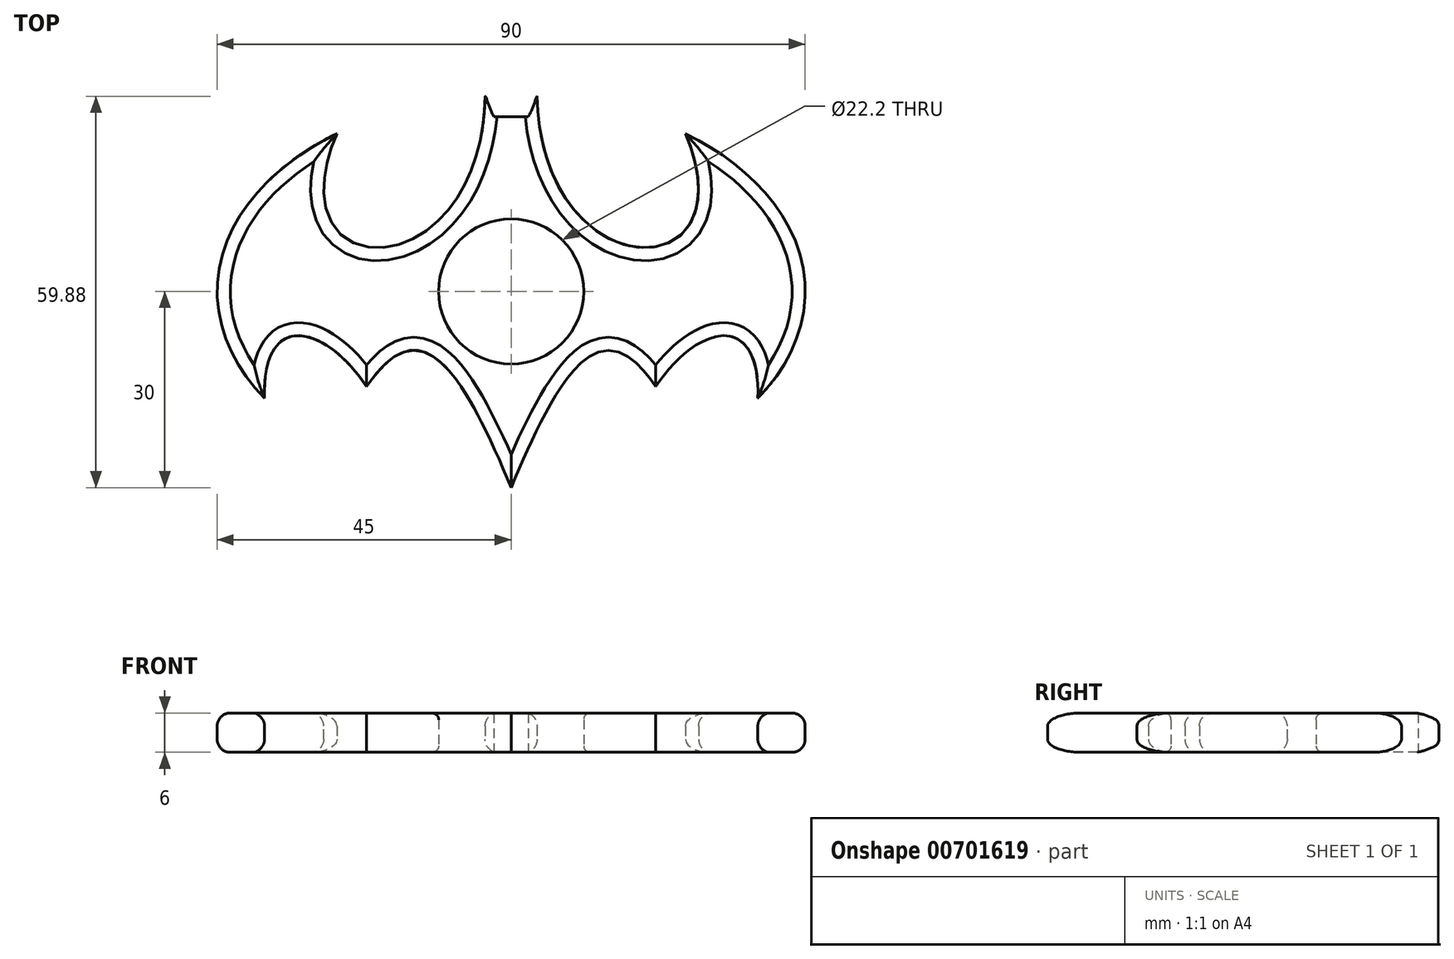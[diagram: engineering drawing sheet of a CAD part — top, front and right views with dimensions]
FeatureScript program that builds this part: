
annotation { "Feature Type Name" : "Feature", "Feature Type Description" : "" }
export const myFeature = defineFeature(function(context is Context, id is Id, definition is map)
    precondition{}
    {
        {
            var Q0;
            Q0=qCreatedBy(makeId("Top.planeOp"),FACE);
            var sketch = newSketch(context, id + "F0", { "sketchPlane" : qUnion([Q0])});
            skCircle(sketch, "E0", {"center": v(0, 0) * mm, "radius": 11.1 * mm});
            skEllipticalArc(sketch, "E1", {});
            skFitSpline(sketch, "E2", {"points": [v(-26.68, 24.16) * mm, v(-3.98, 29.88) * mm], "startDerivative": vector(-30.78, -72.47) * mm, "endDerivative": vector(1.92, 89.65) * mm});
            skFitSpline(sketch, "E3", {"points": [v(-3.98, 29.88) * mm, v(-2.62, 26.73) * mm], "startDerivative": vector(0.9, -0.78) * mm, "endDerivative": vector(3.17, -5.82) * mm});
            skLineSegment(sketch, "E4", {"start": v(-2.62, 26.73) * mm, "end": v(0, 26.73) * mm});
            skFitSpline(sketch, "E5", {"points": [v(-37.75, -16.33) * mm, v(-22.12, -14.55) * mm], "startDerivative": vector(-1.4, 39.24) * mm, "endDerivative": vector(20.6, -30.22) * mm});
            skFitSpline(sketch, "E6", {"points": [v(-22.12, -14.55) * mm, v(0, -30) * mm], "startDerivative": vector(24.27, 35.99) * mm, "endDerivative": vector(23.73, -57) * mm});
            skPoint(sketch, "E7", {"position": v(-45, 0) * mm});
            skPoint(sketch, "E8", {"position": v(0, 30) * mm});
            skFitSpline(sketch, "E9.MirrorCS", {"points": [v(3.98, 29.88) * mm, v(2.62, 26.73) * mm], "startDerivative": vector(-0.9, -0.78) * mm, "endDerivative": vector(-3.17, -5.82) * mm});
            skPoint(sketch, "E10.MirrorP", {"position": v(45, 0) * mm});
            skFitSpline(sketch, "E11.MirrorCS", {"points": [v(22.12, -14.55) * mm, v(0, -30) * mm], "startDerivative": vector(-24.27, 35.99) * mm, "endDerivative": vector(-23.73, -57) * mm});
            skFitSpline(sketch, "E12.MirrorCS", {"points": [v(37.75, -16.33) * mm, v(22.12, -14.55) * mm], "startDerivative": vector(1.4, 39.24) * mm, "endDerivative": vector(-20.6, -30.22) * mm});
            skFitSpline(sketch, "E13.MirrorCS", {"points": [v(26.68, 24.16) * mm, v(3.98, 29.88) * mm], "startDerivative": vector(30.78, -72.47) * mm, "endDerivative": vector(-1.92, 89.65) * mm});
            skLineSegment(sketch, "E14.MirrorCS", {"start": v(2.62, 26.73) * mm, "end": v(0, 26.73) * mm});
            skEllipticalArc(sketch, "E15.trimOffspring", {});
            const initialGuessF0  = {"E1": [0, 0, 1, 0, 0.045, 0.03, 2.2055100400062204, 3.717172004093273], "E15.trimOffspring": [0, 0, 1, 0, 0.045, 0.03, 5.707605956676106, 0.9360826135835729]};
            skSetInitialGuess(sketch, initialGuessF0);
            skSolve(sketch);
        }
        {
            var Q0;
            Q0=makeQuery(id+"F0.imprint","IMPRINT",FACE,{"disambiguationData":[TD([[makeQuery(id+"F0.imprint","IMPRINT",EDGE,{"derivedFrom":sQuery(id+"F0.wireOp",EDGE,"E0")}),-1.0]])]});
            extrude(context, id + "F1", {"entities" : qUnion([Q0]), "depth" : 6 * mm, "offsetDistance" : 25 * mm});
        }
        {
            var Q0;
            Q0=makeQuery(id+"F1.opExtrude","CAP_EDGE",EDGE,{"disambiguationData":[OSD([sQuery(id+"F0.wireOp",EDGE,"E5")])],"isStart":false});
            var Q1;
            Q1=makeQuery(id+"F1.opExtrude","CAP_EDGE",EDGE,{"disambiguationData":[OSD([sQuery(id+"F0.wireOp",EDGE,"E6")])],"isStart":false});
            var Q2;
            Q2=makeQuery(id+"F1.opExtrude","CAP_EDGE",EDGE,{"disambiguationData":[OSD([sQuery(id+"F0.wireOp",EDGE,"E1")])],"isStart":false});
            var Q3;
            Q3=makeQuery(id+"F1.opExtrude","CAP_EDGE",EDGE,{"disambiguationData":[OSD([sQuery(id+"F0.wireOp",EDGE,"E2")])],"isStart":false});
            var Q4;
            Q4=makeQuery(id+"F1.opExtrude","CAP_EDGE",EDGE,{"disambiguationData":[OSD([sQuery(id+"F0.wireOp",EDGE,"E13.MirrorCS")])],"isStart":false});
            var Q5;
            Q5=makeQuery(id+"F1.opExtrude","CAP_EDGE",EDGE,{"disambiguationData":[OSD([sQuery(id+"F0.wireOp",EDGE,"E15.trimOffspring")])],"isStart":false});
            var Q6;
            Q6=makeQuery(id+"F1.opExtrude","CAP_EDGE",EDGE,{"disambiguationData":[OSD([sQuery(id+"F0.wireOp",EDGE,"E12.MirrorCS")])],"isStart":false});
            var Q7;
            Q7=makeQuery(id+"F1.opExtrude","CAP_EDGE",EDGE,{"disambiguationData":[OSD([sQuery(id+"F0.wireOp",EDGE,"E11.MirrorCS")])],"isStart":false});
            var Q8;
            Q8=makeQuery(id+"F1.opExtrude","CAP_EDGE",EDGE,{"disambiguationData":[OSD([sQuery(id+"F0.wireOp",EDGE,"E11.MirrorCS")])],"isStart":true});
            var Q9;
            Q9=makeQuery(id+"F1.opExtrude","CAP_EDGE",EDGE,{"disambiguationData":[OSD([sQuery(id+"F0.wireOp",EDGE,"E12.MirrorCS")])],"isStart":true});
            var Q10;
            Q10=makeQuery(id+"F1.opExtrude","CAP_EDGE",EDGE,{"disambiguationData":[OSD([sQuery(id+"F0.wireOp",EDGE,"E15.trimOffspring")])],"isStart":true});
            var Q11;
            Q11=makeQuery(id+"F1.opExtrude","CAP_EDGE",EDGE,{"disambiguationData":[OSD([sQuery(id+"F0.wireOp",EDGE,"E6")])],"isStart":true});
            var Q12;
            Q12=makeQuery(id+"F1.opExtrude","CAP_EDGE",EDGE,{"disambiguationData":[OSD([sQuery(id+"F0.wireOp",EDGE,"E5")])],"isStart":true});
            var Q13;
            Q13=makeQuery(id+"F1.opExtrude","CAP_EDGE",EDGE,{"disambiguationData":[OSD([sQuery(id+"F0.wireOp",EDGE,"E1")])],"isStart":true});
            var Q14;
            Q14=makeQuery(id+"F1.opExtrude","CAP_EDGE",EDGE,{"disambiguationData":[OSD([sQuery(id+"F0.wireOp",EDGE,"E2")])],"isStart":true});
            var Q15;
            Q15=makeQuery(id+"F1.opExtrude","CAP_EDGE",EDGE,{"disambiguationData":[OSD([sQuery(id+"F0.wireOp",EDGE,"E13.MirrorCS")])],"isStart":true});
            fillet(context, id + "F2", {"entities" : qUnion([Q0, Q1, Q2, Q3, Q4, Q5, Q6, Q7, Q8, Q9, Q10, Q11, Q12, Q13, Q14, Q15]), "radius" : 2 * mm, "tangentPropagation" : true, "allowEdgeOverflow" : false});
        }
        {
            var Q0;
            Q0=makeQuery(id+"F1.opExtrude","CAP_EDGE",EDGE,{"disambiguationData":[OSD([sQuery(id+"F0.wireOp",EDGE,"E0")])],"isStart":false});
            var Q1;
            Q1=makeQuery(id+"F1.opExtrude","CAP_EDGE",EDGE,{"disambiguationData":[OSD([sQuery(id+"F0.wireOp",EDGE,"E0")])],"isStart":true});
            fillet(context, id + "F3", {"entities" : qUnion([Q0, Q1]), "radius" : 1 * mm, "tangentPropagation" : true, "allowEdgeOverflow" : false});
        }
    });
